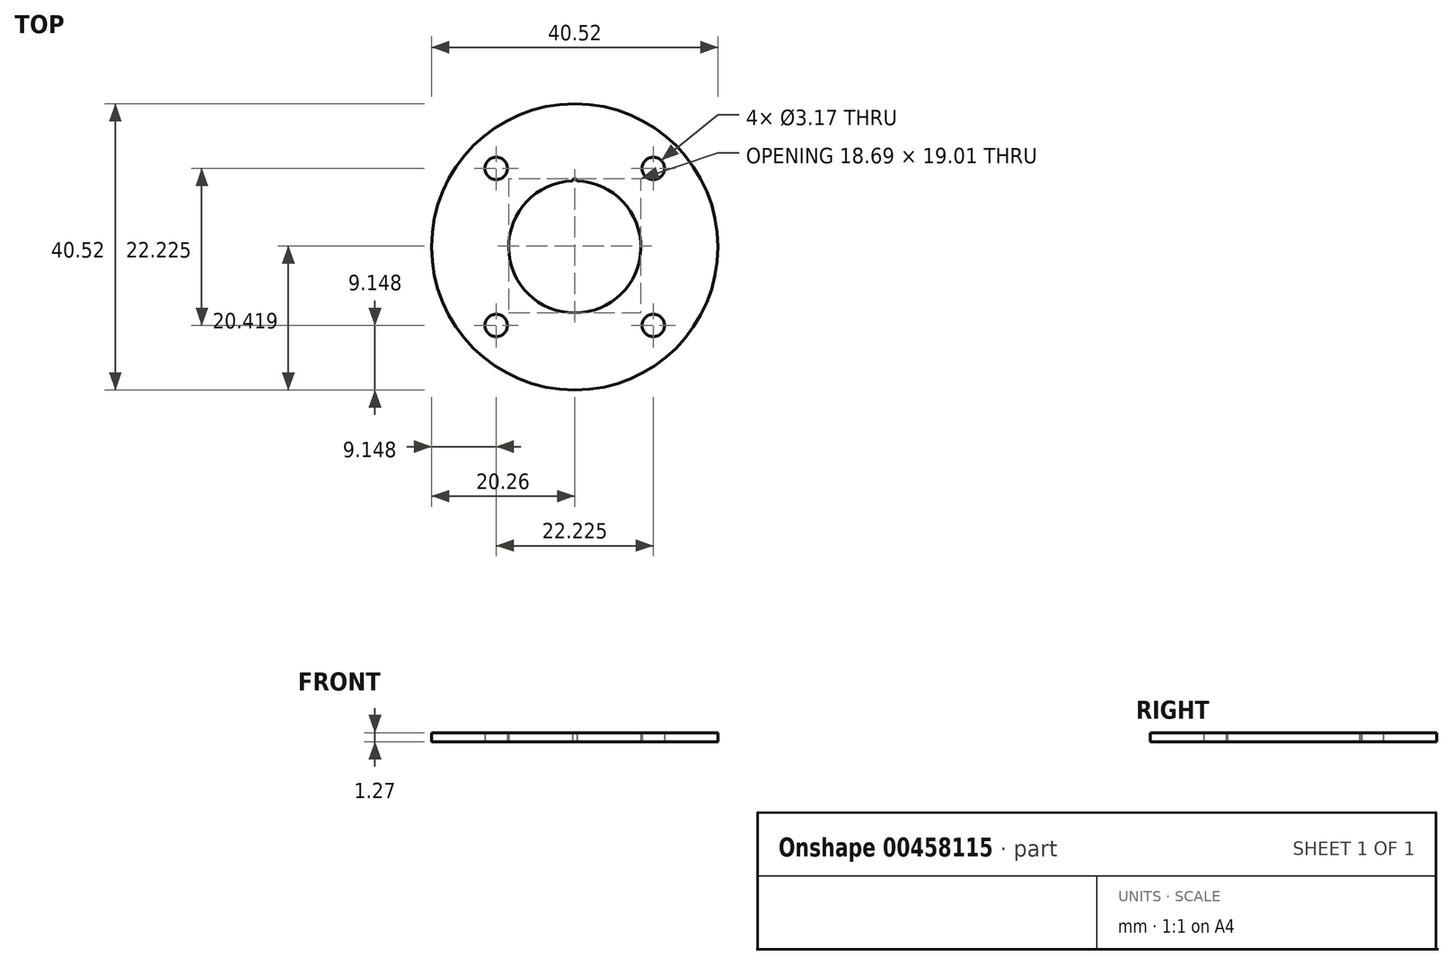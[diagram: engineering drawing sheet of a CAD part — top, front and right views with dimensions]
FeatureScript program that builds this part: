
annotation { "Feature Type Name" : "Feature", "Feature Type Description" : "" }
export const myFeature = defineFeature(function(context is Context, id is Id, definition is map)
    precondition{}
    {
        {
            var Q0;
            Q0=qCreatedBy(makeId("Top.planeOp"),FACE);
            var sketch = newSketch(context, id + "F0", { "sketchPlane" : qUnion([Q0])});
            skCircle(sketch, "E0", {"center": v(0, 0) * mm, "radius": 20.26 * mm});
            skCircle(sketch, "E1", {"center": v(11.11, 11.11) * mm, "radius": 1.59 * mm});
            skCircle(sketch, "E2", {"center": v(-11.11, 11.11) * mm, "radius": 1.59 * mm});
            skCircle(sketch, "E3", {"center": v(-11.11, -11.11) * mm, "radius": 1.59 * mm});
            skCircle(sketch, "E4", {"center": v(11.11, -11.11) * mm, "radius": 1.59 * mm});
            skLineSegment(sketch, "E5", {"start": v(-11.11, 11.11) * mm, "end": v(11.11, 11.11) * mm, "construction": true});
            skLineSegment(sketch, "E6", {"start": v(11.11, 11.11) * mm, "end": v(11.11, -11.11) * mm, "construction": true});
            skLineSegment(sketch, "E7", {"start": v(11.11, -11.11) * mm, "end": v(-11.11, -11.11) * mm, "construction": true});
            skLineSegment(sketch, "E8", {"start": v(-11.11, -11.11) * mm, "end": v(-11.11, 11.11) * mm, "construction": true});
            skCircle(sketch, "E9", {"center": v(0, 0) * mm, "radius": 9.35 * mm});
            skCircle(sketch, "E10", {"center": v(0, 9.35) * mm, "radius": 0.32 * mm});
            skPoint(sketch, "E11", {"position": v(-0.32, 9.34) * mm});
            skPoint(sketch, "E12", {"position": v(0.32, 9.34) * mm});
            skSolve(sketch);
        }
        {
            var Q0;
            Q0=makeQuery(id+"F0.imprint","IMPRINT",FACE,{"disambiguationData":[TD([[makeQuery(id+"F0.imprint","IMPRINT",EDGE,{"derivedFrom":sQuery(id+"F0.wireOp",EDGE,"E0")}),1.0]])]});
            extrude(context, id + "F1", {"entities" : qUnion([Q0]), "depth" : 1.27 * mm});
        }
    });
